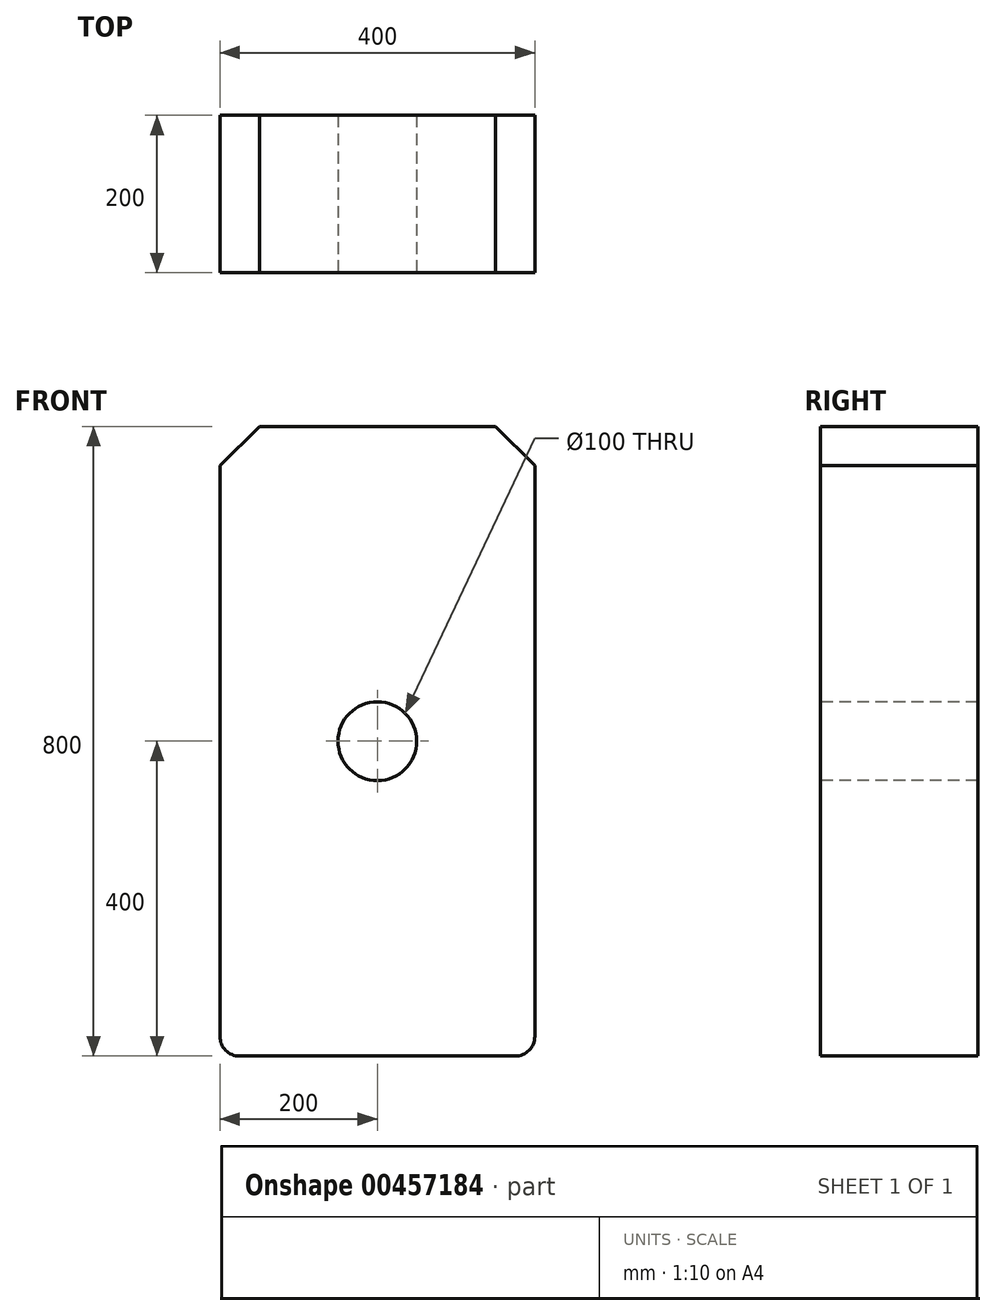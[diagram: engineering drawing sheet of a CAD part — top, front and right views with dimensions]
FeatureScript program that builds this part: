
annotation { "Feature Type Name" : "Feature", "Feature Type Description" : "" }
export const myFeature = defineFeature(function(context is Context, id is Id, definition is map)
    precondition{}
    {
        {
            var Q0;
            Q0=qCreatedBy(makeId("Front.planeOp"),FACE);
            var sketch = newSketch(context, id + "F0", { "sketchPlane" : qUnion([Q0])});
            skLineSegment(sketch, "E0.bottom", {"start": v(200, 400) * mm, "end": v(-200, 400) * mm});
            skLineSegment(sketch, "E0.top", {"start": v(200, -400) * mm, "end": v(-200, -400) * mm});
            skLineSegment(sketch, "E0.left", {"start": v(200, 400) * mm, "end": v(200, -400) * mm});
            skLineSegment(sketch, "E0.right", {"start": v(-200, 400) * mm, "end": v(-200, -400) * mm});
            skPoint(sketch, "E0.middle", {"position": v(0, 0) * mm});
            skSolve(sketch);
        }
        {
            var Q0;
            Q0 = qSketchRegion(id + "F0", true);
            extrude(context, id + "F1", {"entities" : qUnion([Q0]), "depth" : 200 * mm});
        }
        {
            var Q0;
            Q0=makeQuery(id+"F1.opExtrude","SWEPT_EDGE",EDGE,{"disambiguationData":[OSD([sQuery(id+"F0.wireOp",EDGE,"E0.bottom"),sQuery(id+"F0.wireOp",EDGE,"E0.left")])]});
            chamfer(context, id + "F2", {"entities" : qUnion([Q0]), "width" : 50 * mm, "tangentPropagation" : true});
        }
        {
            var Q0;
            Q0=makeQuery(id+"F1.opExtrude","SWEPT_EDGE",EDGE,{"disambiguationData":[OSD([sQuery(id+"F0.wireOp",EDGE,"E0.bottom"),sQuery(id+"F0.wireOp",EDGE,"E0.right")])]});
            chamfer(context, id + "F3", {"entities" : qUnion([Q0]), "width" : 50 * mm, "tangentPropagation" : true});
        }
        {
            var Q0;
            Q0=makeQuery(id+"F1.opExtrude","SWEPT_EDGE",EDGE,{"disambiguationData":[OSD([sQuery(id+"F0.wireOp",EDGE,"E0.top"),sQuery(id+"F0.wireOp",EDGE,"E0.right")])]});
            fillet(context, id + "F4", {"entities" : qUnion([Q0]), "radius" : 25 * mm, "tangentPropagation" : true, "allowEdgeOverflow" : false});
        }
        {
            var Q0;
            Q0=makeQuery(id+"F1.opExtrude","SWEPT_EDGE",EDGE,{"disambiguationData":[OSD([sQuery(id+"F0.wireOp",EDGE,"E0.top"),sQuery(id+"F0.wireOp",EDGE,"E0.left")])]});
            fillet(context, id + "F5", {"entities" : qUnion([Q0]), "radius" : 25 * mm, "tangentPropagation" : true, "allowEdgeOverflow" : false});
        }
        {
            var Q0;
            Q0=makeQuery(id+"F1.opExtrude","CAP_FACE",FACE,{"disambiguationData":[OSD([sQuery(id+"F0.wireOp",EDGE,"E0.bottom"),sQuery(id+"F0.wireOp",EDGE,"E0.top"),sQuery(id+"F0.wireOp",EDGE,"E0.left"),sQuery(id+"F0.wireOp",EDGE,"E0.right")])],"isStart":false});
            var sketch = newSketch(context, id + "F6", { "sketchPlane" : qUnion([Q0])});
            skCircle(sketch, "E1", {"center": v(0, 0) * mm, "radius": 50 * mm});
            skSolve(sketch);
        }
        {
            var Q0;
            Q0 = qSketchRegion(id + "F6", true);
            var Q1;
            Q1=makeQuery(id+"F6.imprint","IMPRINT",FACE,{"disambiguationData":[TD([[makeQuery(id+"F6.imprint","IMPRINT",EDGE,{"derivedFrom":sQuery(id+"F6.wireOp",EDGE,"E1")}),1.0]])]});
            extrude(context, id + "F7", {"entities" : qUnion([Q0, Q1]), "operationType" : NewBodyOperationType.REMOVE, "oppositeDirection" : true, "depth" : 508 * mm});
        }
    });
